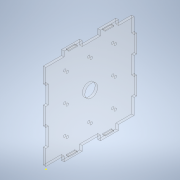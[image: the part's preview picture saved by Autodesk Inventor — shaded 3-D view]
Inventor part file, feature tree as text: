
AUTODESK INVENTOR PART (.ipt)
format: ipt  version: 2021 (Build 250183000, 183)  size: 202,752 bytes
history: native  units: mm
features: sketch x11, hole x9, extrude x1
ambient origin geometry x8: Origin, YZ Plane, XZ Plane, XY Plane, X Axis, Y Axis, Z Axis, Center Point
bodies: Solid1 (feature_tree)
feature tree (21):
  extrude  "Extrusion1"  Depth=10.0mm
  hole  "Hole1"  [1 undecoded]
  hole  "Hole4"  [1 undecoded]
  sketch  "Sketch6"  dims[d54=3.0mm d55=6.0mm d56=4.0mm d57=2.0mm d58=90.0deg d59=8.0mm d60=20.594885mm d61=3.0mm]
  sketch  "Sketch7"  dims[d62=3.0mm d63=6.0mm d64=4.0mm d65=2.0mm d66=90.0deg d67=8.0mm d68=20.594885mm d69=3.0mm]
  hole  "Hole5"  [1 undecoded]
  hole  "Hole6"  [1 undecoded]
  hole  "Hole7"  [1 undecoded]
  hole  "Hole8"  [1 undecoded]
  hole  "Hole9"  [1 undecoded]
  hole  "Hole10"  [1 undecoded]
  hole  "Hole11"  [1 undecoded]
  sketch  "Sketch1"  dims[d4=3.0mm d5=0.0mm d6=10.0mm]
  sketch  "Sketch3"  dims[d7=15.0mm d8=6.0mm d9=4.0mm d10=2.0mm d11=90.0deg d12=8.0mm d13=20.594885mm d45=3.0mm]
  sketch  "Sketch5"  dims[d46=3.0mm d47=6.0mm d48=4.0mm d49=2.0mm d50=90.0deg d51=8.0mm d52=20.594885mm d53=3.0mm]
  sketch  "Sketch8"  dims[d70=3.0mm d71=6.0mm d72=4.0mm d73=2.0mm d74=90.0deg d75=8.0mm d76=20.594885mm d77=3.0mm]
  sketch  "Sketch9"  dims[d78=3.0mm d79=6.0mm d80=4.0mm d81=2.0mm d82=90.0deg d83=8.0mm d84=20.594885mm d85=3.0mm]
  sketch  "Sketch10"  dims[d86=3.0mm d87=6.0mm d88=4.0mm d89=2.0mm d90=90.0deg d91=8.0mm d92=20.594885mm d93=3.0mm]
  sketch  "Sketch11"  dims[d94=3.0mm d95=6.0mm d96=4.0mm d97=2.0mm d98=90.0deg d99=8.0mm d100=20.594885mm d101=3.0mm]
  sketch  "Sketch12"  dims[d102=3.0mm d103=6.0mm d104=4.0mm d105=2.0mm d106=90.0deg d107=8.0mm d108=20.594885mm d109=10.0mm]
  sketch  "Sketch13"  dims[d110=10.0mm d111=1.0mm d112=10.0mm d113=1.0mm d114=10.0mm d20=1.0mm d21=1.0mm d22=1.0mm d23=0.15mm d24=0.25mm d25=0.375mm d26=14.3117mm d27=0.75mm d28=20.594885mm d29=0.0625mm d30=0.75mm d31=0.375mm]
note: 9 required parameter values undecoded (feature->parameter linkage not recoverable at this tier; creation-order binding heuristic only, values carry confidence <= 0.55)
